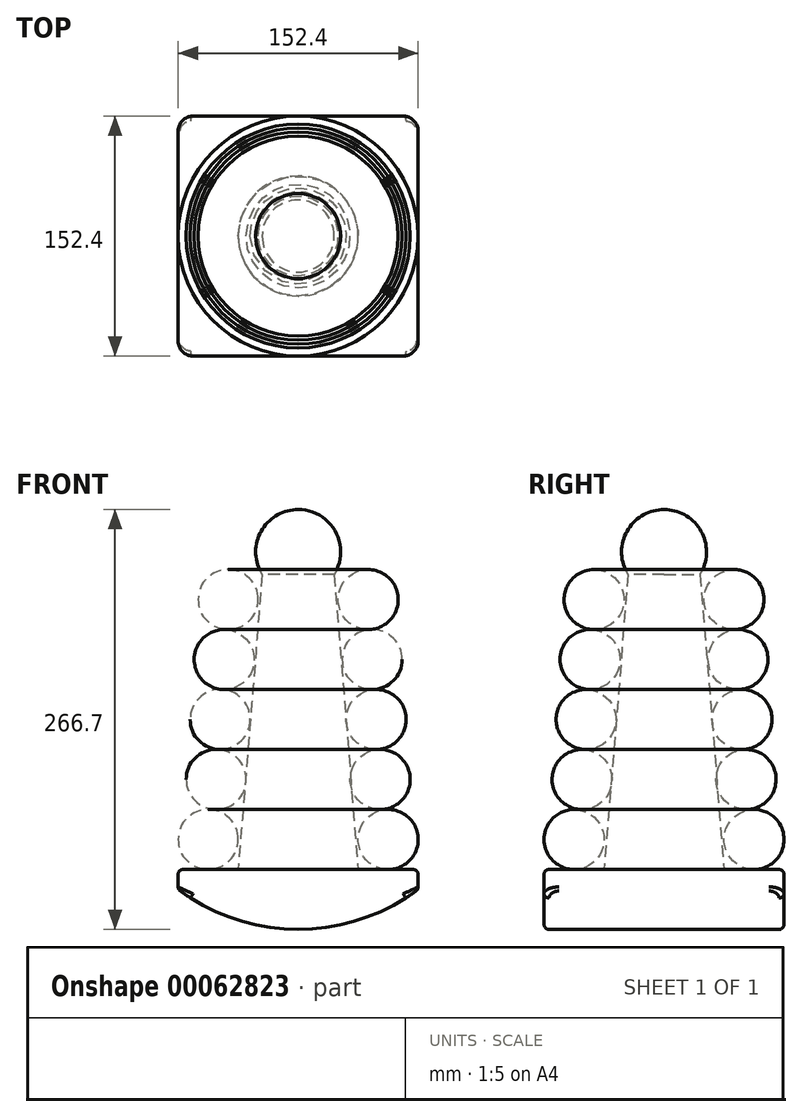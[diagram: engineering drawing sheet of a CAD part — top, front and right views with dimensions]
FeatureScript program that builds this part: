
annotation { "Feature Type Name" : "Feature", "Feature Type Description" : "" }
export const myFeature = defineFeature(function(context is Context, id is Id, definition is map)
    precondition{}
    {
        {
            var Q0;
            Q0=qCreatedBy(makeId("Front.planeOp"),FACE);
            var sketch = newSketch(context, id + "F0", { "sketchPlane" : qUnion([Q0])});
            skLineSegment(sketch, "E0", {"start": v(-76.2, 0) * mm, "end": v(76.2, 0) * mm, "construction": true});
            skLineSegment(sketch, "E1", {"start": v(0, 87.12) * mm, "end": v(0, -116.08) * mm, "construction": true});
            skArc(sketch, "E2", {"start": v(-76.2, 0) * mm, "mid": v(0, -25.4) * mm, "end": v(76.2, 0) * mm});
            skLineSegment(sketch, "E3", {"start": v(-76.2, 0) * mm, "end": v(-76.2, 12.7) * mm});
            skLineSegment(sketch, "E4", {"start": v(-76.2, 12.7) * mm, "end": v(76.2, 12.7) * mm});
            skLineSegment(sketch, "E5", {"start": v(76.2, 12.7) * mm, "end": v(76.2, 0) * mm});
            skSolve(sketch);
        }
        {
            var Q0;
            Q0 = qSketchRegion(id + "F0", true);
            extrude(context, id + "F1", {"entities" : qUnion([Q0]), "endBound" : BoundingType.SYMMETRIC, "depth" : 152.4 * mm});
        }
        {
            var Q0;
            Q0=makeQuery(id+"F1.opExtrude","CAP_EDGE",EDGE,{"disambiguationData":[OSD([sQuery(id+"F0.wireOp",EDGE,"E3")])],"isStart":false});
            var Q1;
            Q1=makeQuery(id+"F1.opExtrude","CAP_EDGE",EDGE,{"disambiguationData":[OSD([sQuery(id+"F0.wireOp",EDGE,"E5")])],"isStart":false});
            var Q2;
            Q2=makeQuery(id+"F1.opExtrude","CAP_EDGE",EDGE,{"disambiguationData":[OSD([sQuery(id+"F0.wireOp",EDGE,"E5")])],"isStart":true});
            var Q3;
            Q3=makeQuery(id+"F1.opExtrude","CAP_EDGE",EDGE,{"disambiguationData":[OSD([sQuery(id+"F0.wireOp",EDGE,"E3")])],"isStart":true});
            fillet(context, id + "F2", {"entities" : qUnion([Q0, Q1, Q2, Q3]), "radius" : 9.52 * mm, "tangentPropagation" : true, "allowEdgeOverflow" : false});
        }
        {
            var Q0;
            Q0=makeQuery(id+"F1.opExtrude","CAP_EDGE",EDGE,{"disambiguationData":[OSD([sQuery(id+"F0.wireOp",EDGE,"E2")])],"isStart":false});
            var Q1;
            Q1=makeQuery(id+"F1.opExtrude","CAP_EDGE",EDGE,{"disambiguationData":[OSD([sQuery(id+"F0.wireOp",EDGE,"E2")])],"isStart":true});
            var Q2;
            Q2=makeQuery(id+"F1.opExtrude","SWEPT_FACE",FACE,{"disambiguationData":[OSD([sQuery(id+"F0.wireOp",EDGE,"E4")])]});
            fillet(context, id + "F3", {"entities" : qUnion([Q0, Q1, Q2]), "radius" : 3.17 * mm, "tangentPropagation" : true, "allowEdgeOverflow" : false});
        }
        {
            var Q0;
            Q0=qCreatedBy(makeId("Front.planeOp"),FACE);
            var sketch = newSketch(context, id + "F4", { "sketchPlane" : qUnion([Q0])});
            skLineSegment(sketch, "E6", {"start": v(0, 12.7) * mm, "end": v(0, 241.3) * mm});
            skLineSegment(sketch, "E7", {"start": v(0, 12.7) * mm, "end": v(-38.1, 12.7) * mm});
            skLineSegment(sketch, "E8", {"start": v(-38.1, 12.7) * mm, "end": v(-22.86, 199.97) * mm});
            skArc(sketch, "E9", {"start": v(0, 241.3) * mm, "mid": v(-23.62, 227.37) * mm, "end": v(-22.86, 199.97) * mm});
            skLineSegment(sketch, "E10", {"start": v(0, 241.3) * mm, "end": v(35.95, 241.3) * mm, "construction": true});
            skLineSegment(sketch, "E11.0", {"start": v(-73.03, 12.7) * mm, "end": v(73.02, 12.7) * mm, "construction": true});
            skPoint(sketch, "E12.orphan", {"position": v(-20.24, 232.16) * mm});
            skSolve(sketch);
        }
        {
            var Q0;
            Q0 = qSketchRegion(id + "F4", true);
            var Q1;
            Q1=sQuery(id+"F4.wireOp",EDGE,"E6");
            revolve(context, id + "F5", {"entities" : qUnion([Q0]), "axis" : qUnion([Q1]), "revolveType" : RevolveType.FULL});
        }
        {
            var Q0;
            Q0=qCreatedBy(makeId("Front.planeOp"),FACE);
            var sketch = newSketch(context, id + "F6", { "sketchPlane" : qUnion([Q0])});
            skCircle(sketch, "E13", {"center": v(-57.15, 31.75) * mm, "radius": 19.05 * mm});
            skLineSegment(sketch, "E14", {"start": v(0, -3.64) * mm, "end": v(0, 153.74) * mm});
            skLineSegment(sketch, "E15.1", {"start": v(-73.03, 12.7) * mm, "end": v(73.02, 12.7) * mm});
            skSolve(sketch);
        }
        {
            var Q0;
            Q0 = qSketchRegion(id + "F6", true);
            var Q1;
            Q1=sQuery(id+"F6.wireOp",EDGE,"E14");
            revolve(context, id + "F7", {"entities" : qUnion([Q0]), "axis" : qUnion([Q1]), "revolveType" : RevolveType.FULL});
        }
        {
            var Q0;
            Q0=qCreatedBy(makeId("Front.planeOp"),FACE);
            var sketch = newSketch(context, id + "F8", { "sketchPlane" : qUnion([Q0])});
            skLineSegment(sketch, "E16", {"start": v(0, 0) * mm, "end": v(0, 170.76) * mm, "construction": true});
            skCircle(sketch, "E17", {"center": v(-52.07, 69.85) * mm, "radius": 19.05 * mm});
            skLineSegment(sketch, "E18", {"start": v(12.3, 50.8) * mm, "end": v(-172.25, 50.8) * mm, "construction": true});
            skSolve(sketch);
        }
        {
            var Q0;
            Q0 = qSketchRegion(id + "F8", true);
            var Q1;
            Q1=sQuery(id+"F8.wireOp",EDGE,"E16");
            revolve(context, id + "F9", {"entities" : qUnion([Q0]), "axis" : qUnion([Q1]), "revolveType" : RevolveType.FULL});
        }
        {
            var Q0;
            Q0=qCreatedBy(makeId("Front.planeOp"),FACE);
            var sketch = newSketch(context, id + "F10", { "sketchPlane" : qUnion([Q0])});
            skLineSegment(sketch, "E19", {"start": v(0, 0) * mm, "end": v(0, 147.29) * mm, "construction": true});
            skLineSegment(sketch, "E20", {"start": v(-148.19, 88.9) * mm, "end": v(90.27, 88.9) * mm, "construction": true});
            skCircle(sketch, "E21", {"center": v(-49.53, 107.95) * mm, "radius": 19.05 * mm});
            skSolve(sketch);
        }
        {
            var Q0;
            Q0=makeQuery(id+"F10.imprint","IMPRINT",FACE,{"disambiguationData":[TD([[makeQuery(id+"F10.imprint","IMPRINT",EDGE,{"derivedFrom":sQuery(id+"F10.wireOp",EDGE,"E21")}),1.0]])]});
            var Q1;
            Q1=sQuery(id+"F10.wireOp",EDGE,"E19");
            revolve(context, id + "F11", {"entities" : qUnion([Q0]), "axis" : qUnion([Q1]), "revolveType" : RevolveType.FULL});
        }
        {
            var Q0;
            Q0=qCreatedBy(makeId("Front.planeOp"),FACE);
            var sketch = newSketch(context, id + "F12", { "sketchPlane" : qUnion([Q0])});
            skLineSegment(sketch, "E22", {"start": v(0, 120.14) * mm, "end": v(0, -63.32) * mm, "construction": true});
            skLineSegment(sketch, "E23", {"start": v(-154.3, 127) * mm, "end": v(90.44, 127) * mm, "construction": true});
            skCircle(sketch, "E24", {"center": v(-47, 146.05) * mm, "radius": 19.05 * mm});
            skSolve(sketch);
        }
        {
            var Q0;
            Q0 = qSketchRegion(id + "F12", true);
            var Q1;
            Q1=sQuery(id+"F12.wireOp",EDGE,"E22");
            revolve(context, id + "F13", {"entities" : qUnion([Q0]), "axis" : qUnion([Q1]), "revolveType" : RevolveType.FULL});
        }
        {
            var Q0;
            Q0=qCreatedBy(makeId("Front.planeOp"),FACE);
            var sketch = newSketch(context, id + "F14", { "sketchPlane" : qUnion([Q0])});
            skLineSegment(sketch, "E25", {"start": v(0, 0) * mm, "end": v(0, 282.6) * mm, "construction": true});
            skLineSegment(sketch, "E26", {"start": v(-272.76, 165.1) * mm, "end": v(156.77, 165.1) * mm, "construction": true});
            skCircle(sketch, "E27", {"center": v(-44.45, 184.15) * mm, "radius": 19.05 * mm});
            skSolve(sketch);
        }
        {
            var Q0;
            Q0 = qSketchRegion(id + "F14", true);
            var Q1;
            Q1=sQuery(id+"F14.wireOp",EDGE,"E25");
            revolve(context, id + "F15", {"entities" : qUnion([Q0]), "axis" : qUnion([Q1]), "revolveType" : RevolveType.FULL});
        }
    });
